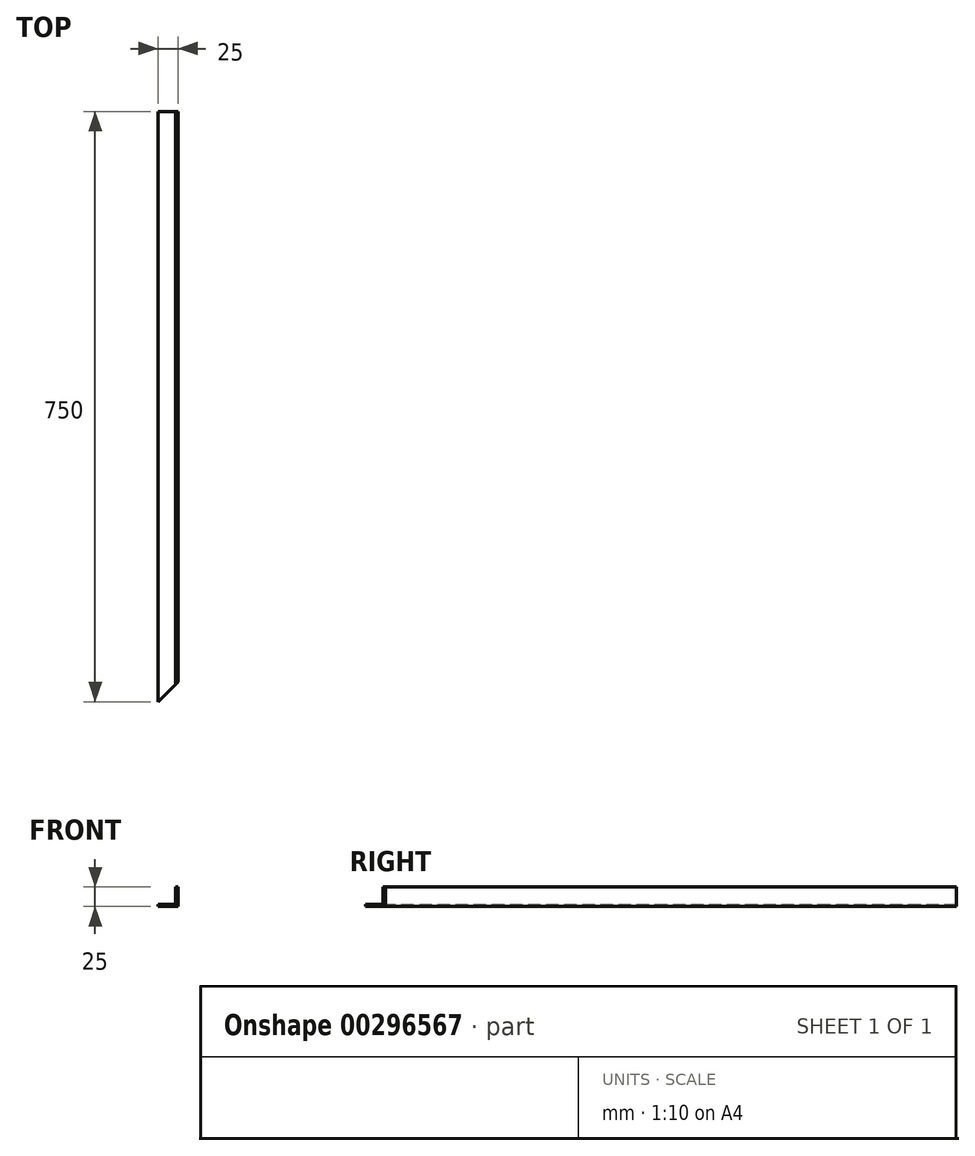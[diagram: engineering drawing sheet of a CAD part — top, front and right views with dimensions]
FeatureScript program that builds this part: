
annotation { "Feature Type Name" : "Feature", "Feature Type Description" : "" }
export const myFeature = defineFeature(function(context is Context, id is Id, definition is map)
    precondition{}
    {
        {
            var Q0;
            Q0=qCreatedBy(makeId("Front.planeOp"),FACE);
            var sketch = newSketch(context, id + "F0", { "sketchPlane" : qUnion([Q0])});
            skLineSegment(sketch, "E0", {"start": v(-16.97, -5.98) * mm, "end": v(5.03, -5.98) * mm});
            skLineSegment(sketch, "E1", {"start": v(5.03, -5.98) * mm, "end": v(5.03, 16.02) * mm});
            skLineSegment(sketch, "E2.0", {"start": v(8.03, -8.98) * mm, "end": v(8.03, 16.02) * mm});
            skLineSegment(sketch, "E2.1", {"start": v(-16.97, -8.98) * mm, "end": v(8.03, -8.98) * mm});
            skLineSegment(sketch, "E3", {"start": v(5.03, 16.02) * mm, "end": v(8.03, 16.02) * mm});
            skLineSegment(sketch, "E4", {"start": v(-16.97, -5.98) * mm, "end": v(-16.97, -8.98) * mm});
            skSolve(sketch);
        }
        {
            var Q0;
            Q0=makeQuery(id+"F0.imprint","IMPRINT",FACE,{"disambiguationData":[TD([[makeQuery(id+"F0.imprint","IMPRINT",EDGE,{"derivedFrom":sQuery(id+"F0.wireOp",EDGE,"E0")}),-1.0]])]});
            extrude(context, id + "F1", {"entities" : qUnion([Q0]), "depth" : 750 * mm});
        }
        {
            var Q0;
            Q0=makeQuery(id+"F1.opExtrude","SWEPT_FACE",FACE,{"disambiguationData":[OSD([sQuery(id+"F0.wireOp",EDGE,"E2.1")])]});
            var sketch = newSketch(context, id + "F2", { "sketchPlane" : qUnion([Q0])});
            skLineSegment(sketch, "E5", {"start": v(-16.97, 750) * mm, "end": v(8.03, 725) * mm});
            skLineSegment(sketch, "E6", {"start": v(8.03, 725) * mm, "end": v(8.03, 750) * mm});
            skSolve(sketch);
        }
        {
            var Q0;
            Q0=makeQuery(id+"F2.imprint","IMPRINT",FACE,{"disambiguationData":[TD([[makeQuery(id+"F2.imprint","IMPRINT",EDGE,{"derivedFrom":sQuery(id+"F2.wireOp",EDGE,"E5")}),1.0]])]});
            extrude(context, id + "F3", {"entities" : qUnion([Q0]), "operationType" : NewBodyOperationType.REMOVE, "oppositeDirection" : true, "depth" : 25 * mm});
        }
    });
